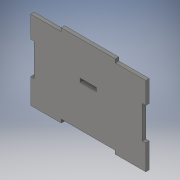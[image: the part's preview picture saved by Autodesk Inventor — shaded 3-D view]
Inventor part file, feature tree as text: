
AUTODESK INVENTOR PART (.ipt)
format: ipt  version: 2019 (Build 230136000, 136)  size: 139,264 bytes
history: native  units: mm
features: other x1, extrude x1, sketch x1
ambient origin geometry x8: Origin, YZ Plane, XZ Plane, XY Plane, X Axis, Y Axis, Z Axis, Center Point
bodies: Body1 (feature_tree)
feature tree (3):
  other  "Sólido1"
  extrude  "Extrusión1"  Depth=73.18mm
  sketch  "Boceto1"  dims[d0=106.36mm d3=73.18mm d4=3.18mm d5=50.0mm d6=25.0mm d8=30.0mm d9=30.0mm d10=3.18mm d11=20.0mm d12=20.0mm d13=50.0mm d14=25.0mm d17=15.0mm d18=3.18mm d19=40.0mm d20=7.5mm d21=3.18mm d22=0.0mm]
